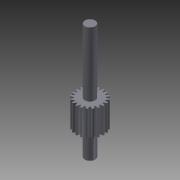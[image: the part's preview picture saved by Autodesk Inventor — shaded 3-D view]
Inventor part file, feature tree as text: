
AUTODESK INVENTOR PART (.ipt)
format: ipt  version: 2011 (Build 150239000, 239)  size: 217,088 bytes
history: native  units: mm (DEFAULTED — no unit token found)
features: sketch x4, extrude x3, plane x3, other x3
ambient origin geometry x8: Origin, YZ Plane, XZ Plane, XY Plane, X Axis, Y Axis, Z Axis, Center Point
bodies: Solid1 (feature_tree)
feature tree (13):
  extrude  "Extrusion1"  Depth=5.0mm TaperAngle=0.0deg
  plane  "Work Plane2"
  plane  "Work Plane8"
  plane  "Work Plane9"
  other  "Spur Gear"
  extrude  "Extrusion2"  Depth=10.0mm TaperAngle=0.0deg
  extrude  "Extrusion3"  Depth=1.570796mm TaperAngle=0.0deg
  sketch  "Sketch1"  dims[d0=5.5mm d1=5.0mm d2=0.0mm]
  sketch  "Sketch2"  dims[d3=5.0mm d4=10.0mm d5=0.0mm]
  other  "Srf1"
  sketch  "Sketch3"  dims[d16=10.0mm d17=0.0mm d34=1.570796mm]
  sketch  "Sketch4"  dims[d39=0.0mm d41=0.0mm d43=10.0mm d46=10.0mm d47=0.0mm d48=0.0mm d49=2.0mm d50=12.5mm d51=0.0mm d52=2.0mm d53=5.0mm d54=0.0mm]
  other  "Pitch Diameter"
